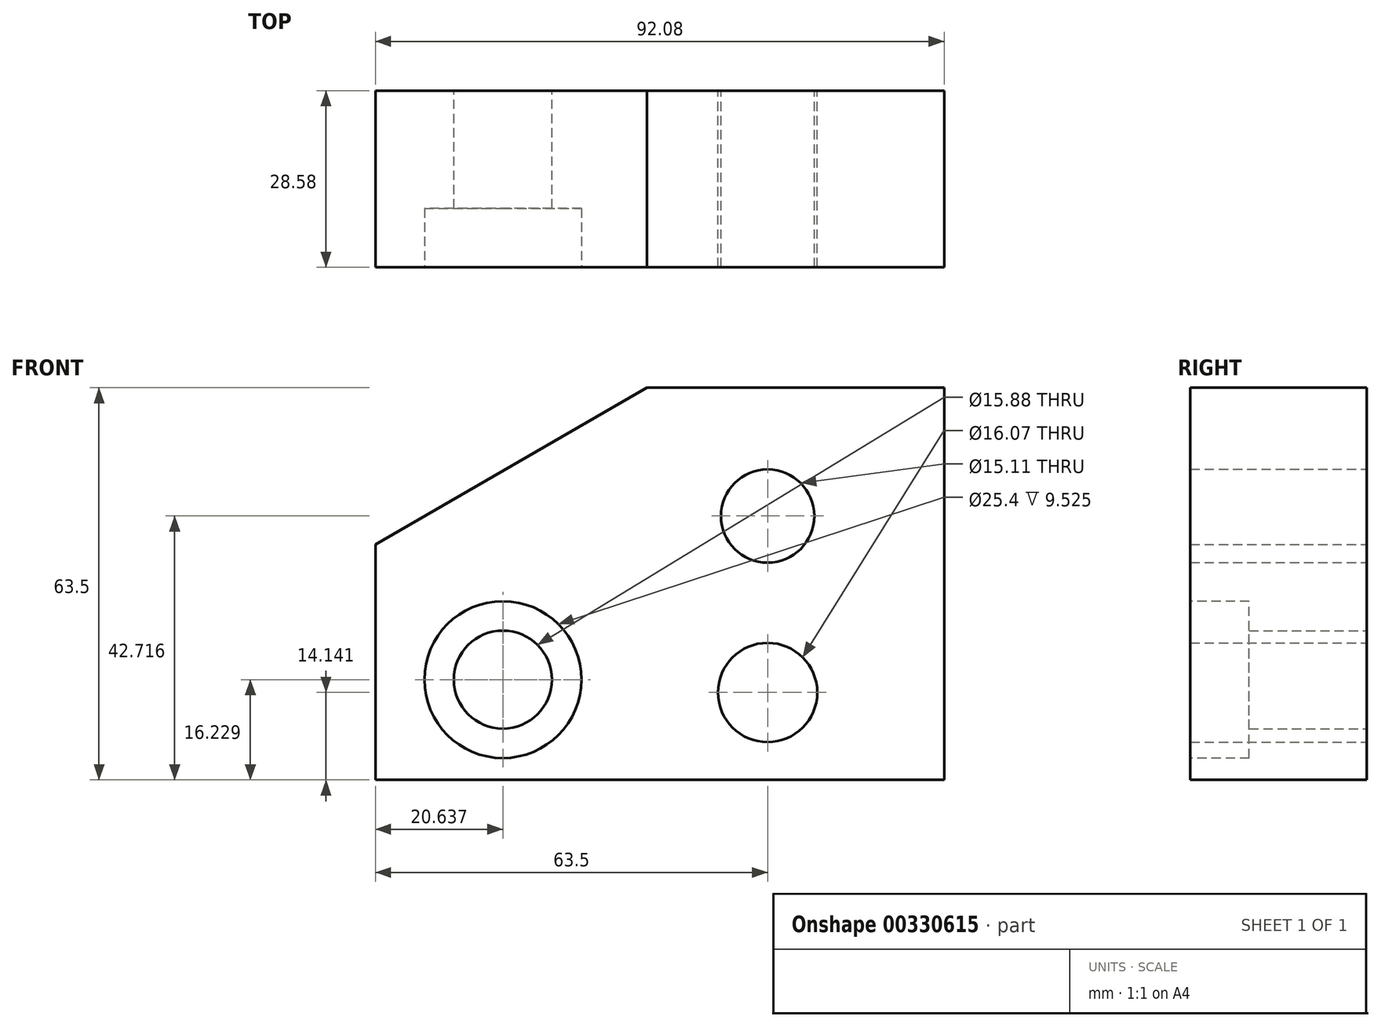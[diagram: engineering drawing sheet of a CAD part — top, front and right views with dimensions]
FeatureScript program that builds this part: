
annotation { "Feature Type Name" : "Feature", "Feature Type Description" : "" }
export const myFeature = defineFeature(function(context is Context, id is Id, definition is map)
    precondition{}
    {
        {
            var Q0;
            Q0=qCreatedBy(makeId("Front.planeOp"),FACE);
            var sketch = newSketch(context, id + "F0", { "sketchPlane" : qUnion([Q0])});
            skLineSegment(sketch, "E0", {"start": v(0, 0) * mm, "end": v(0, 0) * mm});
            skLineSegment(sketch, "E1", {"start": v(0, 0) * mm, "end": v(92.08, 0) * mm});
            skPoint(sketch, "E1.endSnap0", {"position": v(0, 0) * mm});
            skLineSegment(sketch, "E2", {"start": v(92.08, 0) * mm, "end": v(92.08, 63.5) * mm});
            skLineSegment(sketch, "E3", {"start": v(0, 0) * mm, "end": v(0, 38.1) * mm});
            skLineSegment(sketch, "E4", {"start": v(92.08, 63.5) * mm, "end": v(44, 63.5) * mm});
            skLineSegment(sketch, "E5", {"start": v(0, 38.1) * mm, "end": v(44, 63.5) * mm});
            skCircle(sketch, "E6", {"center": v(63.5, 14.14) * mm, "radius": 8.03 * mm});
            skCircle(sketch, "E7", {"center": v(63.5, 42.72) * mm, "radius": 7.55 * mm});
            skCircle(sketch, "E8", {"center": v(20.64, 16.23) * mm, "radius": 7.94 * mm});
            skSolve(sketch);
        }
        {
            var Q0;
            Q0 = qSketchRegion(id + "F0", true);
            extrude(context, id + "F1", {"entities" : qUnion([Q0]), "depth" : 28.57 * mm});
        }
        {
            var Q0;
            Q0=makeQuery(id+"F1.opExtrude","CAP_FACE",FACE,{"disambiguationData":[OSD([sQuery(id+"F0.wireOp",EDGE,"E1"),sQuery(id+"F0.wireOp",EDGE,"E2"),sQuery(id+"F0.wireOp",EDGE,"E3"),sQuery(id+"F0.wireOp",EDGE,"E4"),sQuery(id+"F0.wireOp",EDGE,"E5"),sQuery(id+"F0.wireOp",EDGE,"E6"),sQuery(id+"F0.wireOp",EDGE,"E7"),sQuery(id+"F0.wireOp",EDGE,"E8")])],"isStart":false});
            var sketch = newSketch(context, id + "F2", { "sketchPlane" : qUnion([Q0])});
            skCircle(sketch, "E9", {"center": v(20.64, 16.23) * mm, "radius": 12.7 * mm});
            skSolve(sketch);
        }
        {
            var Q0;
            Q0 = qSketchRegion(id + "F2", true);
            extrude(context, id + "F3", {"entities" : qUnion([Q0]), "operationType" : NewBodyOperationType.REMOVE, "oppositeDirection" : true, "depth" : 9.52 * mm});
        }
    });
